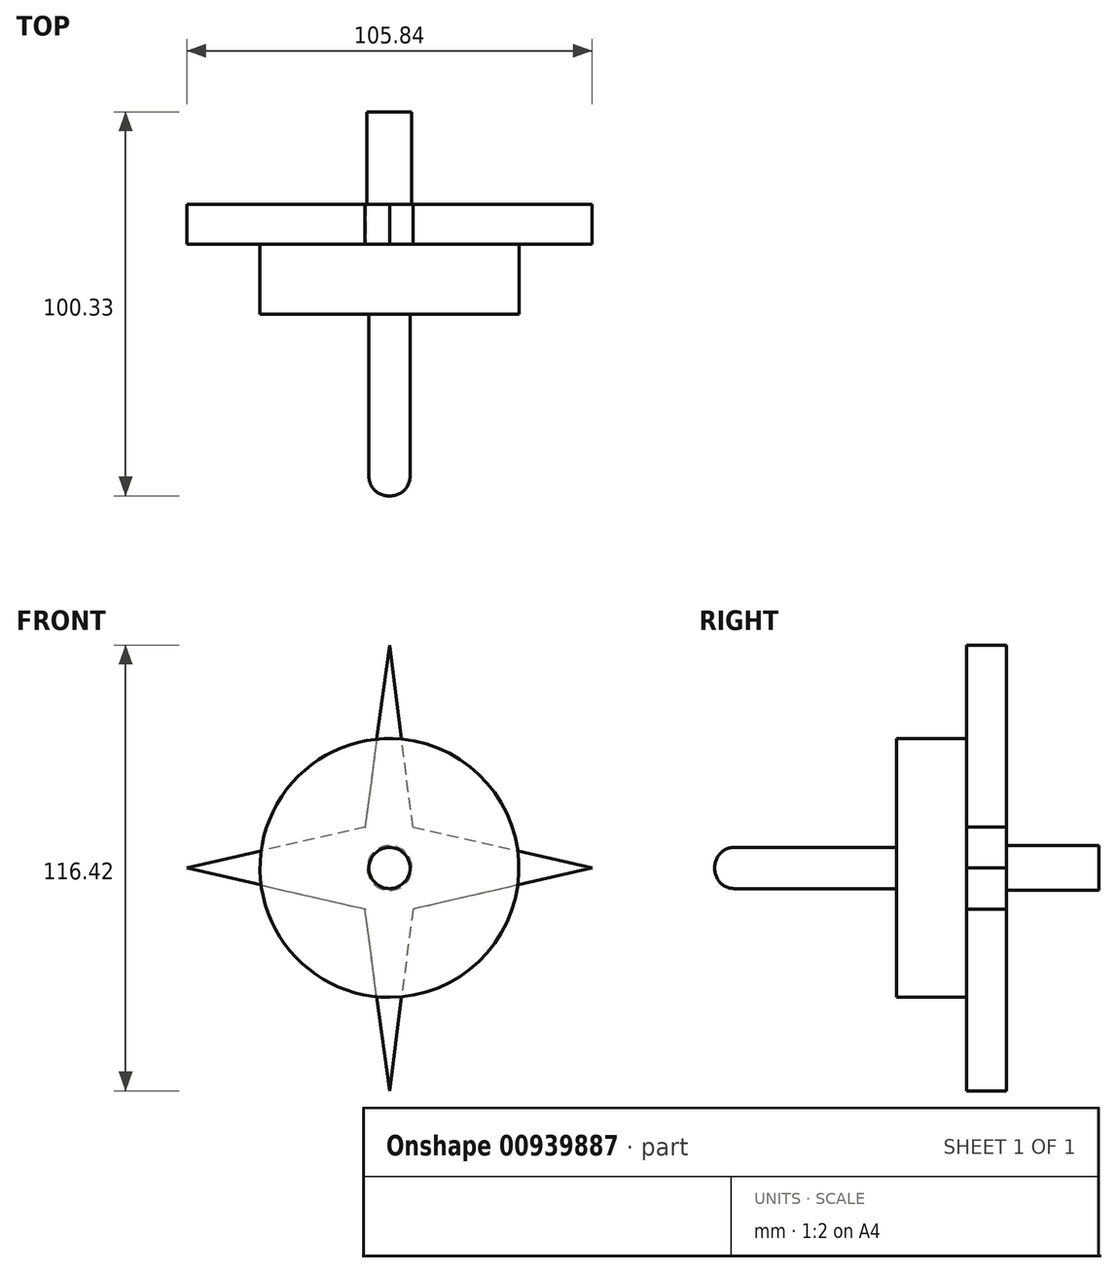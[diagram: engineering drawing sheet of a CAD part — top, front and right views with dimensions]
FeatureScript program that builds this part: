
annotation { "Feature Type Name" : "Feature", "Feature Type Description" : "" }
export const myFeature = defineFeature(function(context is Context, id is Id, definition is map)
    precondition{}
    {
        {
            var Q0;
            Q0=qCreatedBy(makeId("Front.planeOp"),FACE);
            var sketch = newSketch(context, id + "F0", { "sketchPlane" : qUnion([Q0])});
            skCircle(sketch, "E0", {"center": v(0, 0) * mm, "radius": 33.8 * mm});
            skSolve(sketch);
        }
        {
            var Q0;
            Q0 = qSketchRegion(id + "F0", true);
            extrude(context, id + "F1", {"entities" : qUnion([Q0]), "depth" : 18.29 * mm, "offsetDistance" : 25.4 * mm});
        }
        {
            var Q0;
            Q0=makeQuery(id+"F1.opExtrude","CAP_FACE",FACE,{"disambiguationData":[OSD([sQuery(id+"F0.wireOp",EDGE,"E0")])],"isStart":false});
            var sketch = newSketch(context, id + "F2", { "sketchPlane" : qUnion([Q0])});
            skCircle(sketch, "E1", {"center": v(0, 0) * mm, "radius": 5.37 * mm});
            skSolve(sketch);
        }
        {
            var Q0;
            Q0 = qSketchRegion(id + "F2", true);
            extrude(context, id + "F3", {"entities" : qUnion([Q0]), "operationType" : NewBodyOperationType.ADD, "depth" : 47.5 * mm, "offsetDistance" : 25.4 * mm});
        }
        {
            var Q0;
            Q0=makeQuery(id+"F3.opExtrude","CAP_EDGE",EDGE,{"disambiguationData":[OSD([sQuery(id+"F2.wireOp",EDGE,"E1")])],"isStart":false});
            fillet(context, id + "F4", {"entities" : qUnion([Q0]), "radius" : 5.08 * mm, "tangentPropagation" : true, "allowEdgeOverflow" : false});
        }
        {
            var Q0;
            Q0=makeQuery(id+"F1.opExtrude","CAP_FACE",FACE,{"disambiguationData":[OSD([sQuery(id+"F0.wireOp",EDGE,"E0")])],"isStart":true});
            var sketch = newSketch(context, id + "F5", { "sketchPlane" : qUnion([Q0])});
            skCircle(sketch, "E2", {"center": v(0, 0) * mm, "radius": 5.84 * mm});
            skSolve(sketch);
        }
        {
            var Q0;
            Q0 = qSketchRegion(id + "F5", true);
            extrude(context, id + "F6", {"entities" : qUnion([Q0]), "operationType" : NewBodyOperationType.ADD, "depth" : 34.54 * mm, "offsetDistance" : 25.4 * mm});
        }
        {
            var Q0;
            Q0=makeQuery(id+"F1.opExtrude","CAP_FACE",FACE,{"disambiguationData":[OSD([sQuery(id+"F0.wireOp",EDGE,"E0")])],"isStart":true});
            var sketch = newSketch(context, id + "F7", { "sketchPlane" : qUnion([Q0])});
            skLineSegment(sketch, "E3", {"start": v(-6.13, -10.76) * mm, "end": v(0, -58.2) * mm});
            skLineSegment(sketch, "E4", {"start": v(0, -58.2) * mm, "end": v(6.39, -10.76) * mm});
            skLineSegment(sketch, "E5", {"start": v(6.39, -10.76) * mm, "end": v(-6.13, -10.76) * mm});
            skLineSegment(sketch, "E6.MirrorCS", {"start": v(6.39, 10.76) * mm, "end": v(-6.13, 10.76) * mm});
            skLineSegment(sketch, "E7.MirrorCS", {"start": v(0, 58.2) * mm, "end": v(6.39, 10.76) * mm});
            skLineSegment(sketch, "E8.MirrorCS", {"start": v(-6.13, 10.76) * mm, "end": v(0, 58.2) * mm});
            skLineSegment(sketch, "E9", {"start": v(-6.13, 10.76) * mm, "end": v(-52.92, 0) * mm});
            skLineSegment(sketch, "E10", {"start": v(-52.92, 0) * mm, "end": v(-6.13, -10.76) * mm});
            skLineSegment(sketch, "E11", {"start": v(-6.13, 10.76) * mm, "end": v(-6.13, -10.76) * mm});
            skLineSegment(sketch, "E12.MirrorCS", {"start": v(6.13, 10.76) * mm, "end": v(6.13, -10.76) * mm});
            skLineSegment(sketch, "E13.MirrorCS", {"start": v(6.13, 10.76) * mm, "end": v(52.92, 0) * mm});
            skLineSegment(sketch, "E14.MirrorCS", {"start": v(52.92, 0) * mm, "end": v(6.13, -10.76) * mm});
            skSolve(sketch);
        }
        {
            var Q0;
            {var subQ0=sQuery(id+"F7.wireOp",EDGE,"E11");Q0=makeQuery(id+"F7.imprint","IMPRINT",FACE,{"disambiguationData":[TD([[makeQuery(id+"F7.imprint","IMPRINT",EDGE,{"derivedFrom":subQ0}),-1.0]])]});}
            var Q1;
            {var subQ0=sQuery(id+"F7.wireOp",EDGE,"E10");var subQ1=sQuery(id+"F7.wireOp",EDGE,"E9");var subQ2=makeQuery(id+"F7.imprint","INTERSECT",VERTEX,{"derivedFrom":[subQ1,subQ0]});Q1=makeQuery(id+"F7.imprint","IMPRINT",FACE,{"disambiguationData":[TD([[makeQuery(id+"F7.imprint","IMPRINT",EDGE,{"disambiguationData":[TD([[subQ2,1.0]])],"derivedFrom":subQ1}),1.0]])]});}
            var Q2;
            {var subQ0=sQuery(id+"F7.wireOp",EDGE,"E5");var subQ1=sQuery(id+"F7.wireOp",EDGE,"E4");var subQ2=makeQuery(id+"F7.imprint","INTERSECT",VERTEX,{"derivedFrom":[subQ1,subQ0]});Q2=makeQuery(id+"F7.imprint","IMPRINT",FACE,{"disambiguationData":[TD([[makeQuery(id+"F7.imprint","IMPRINT",EDGE,{"disambiguationData":[TD([[subQ2,1.0]])],"derivedFrom":subQ1}),1.0]])]});}
            var Q3;
            {var subQ0=sQuery(id+"F7.wireOp",EDGE,"E4");var subQ1=sQuery(id+"F7.wireOp",EDGE,"E3");var subQ2=makeQuery(id+"F7.imprint","INTERSECT",VERTEX,{"derivedFrom":[subQ1,subQ0]});Q3=makeQuery(id+"F7.imprint","IMPRINT",FACE,{"disambiguationData":[TD([[makeQuery(id+"F7.imprint","IMPRINT",EDGE,{"disambiguationData":[TD([[subQ2,1.0]])],"derivedFrom":subQ1}),1.0]])]});}
            var Q4;
            {var subQ0=sQuery(id+"F7.wireOp",EDGE,"E11");Q4=makeQuery(id+"F7.imprint","IMPRINT",FACE,{"disambiguationData":[TD([[makeQuery(id+"F7.imprint","IMPRINT",EDGE,{"derivedFrom":subQ0}),1.0]])]});}
            var Q5;
            {var subQ0=sQuery(id+"F7.wireOp",EDGE,"E12.MirrorCS");Q5=makeQuery(id+"F7.imprint","IMPRINT",FACE,{"disambiguationData":[TD([[makeQuery(id+"F7.imprint","IMPRINT",EDGE,{"derivedFrom":subQ0}),1.0]])]});}
            var Q6;
            {var subQ0=sQuery(id+"F7.wireOp",EDGE,"E14.MirrorCS");var subQ1=sQuery(id+"F7.wireOp",EDGE,"E13.MirrorCS");var subQ2=makeQuery(id+"F7.imprint","INTERSECT",VERTEX,{"derivedFrom":[subQ1,subQ0]});Q6=makeQuery(id+"F7.imprint","IMPRINT",FACE,{"disambiguationData":[TD([[makeQuery(id+"F7.imprint","IMPRINT",EDGE,{"disambiguationData":[TD([[subQ2,1.0]])],"derivedFrom":subQ1}),-1.0]])]});}
            var Q7;
            {var subQ1=sQuery(id+"F7.wireOp",EDGE,"E6.MirrorCS");var subQ5=sQuery(id+"F7.wireOp",EDGE,"E7.MirrorCS");var subQ6=makeQuery(id+"F7.imprint","INTERSECT",VERTEX,{"derivedFrom":[subQ1,subQ5]});Q7=makeQuery(id+"F7.imprint","IMPRINT",FACE,{"disambiguationData":[TD([[makeQuery(id+"F7.imprint","IMPRINT",EDGE,{"disambiguationData":[TD([[subQ6,1.0]])],"derivedFrom":subQ5}),-1.0]])]});}
            var Q8;
            {var subQ0=sQuery(id+"F7.wireOp",EDGE,"E8.MirrorCS");var subQ1=sQuery(id+"F7.wireOp",EDGE,"E7.MirrorCS");var subQ2=makeQuery(id+"F7.imprint","INTERSECT",VERTEX,{"derivedFrom":[subQ1,subQ0]});Q8=makeQuery(id+"F7.imprint","IMPRINT",FACE,{"disambiguationData":[TD([[makeQuery(id+"F7.imprint","IMPRINT",EDGE,{"disambiguationData":[TD([[subQ2,-1.0]])],"derivedFrom":subQ1}),-1.0]])]});}
            extrude(context, id + "F8", {"entities" : qUnion([Q0, Q1, Q2, Q3, Q4, Q5, Q6, Q7, Q8]), "operationType" : NewBodyOperationType.ADD, "depth" : 10.4 * mm, "offsetDistance" : 25.4 * mm});
        }
    });
